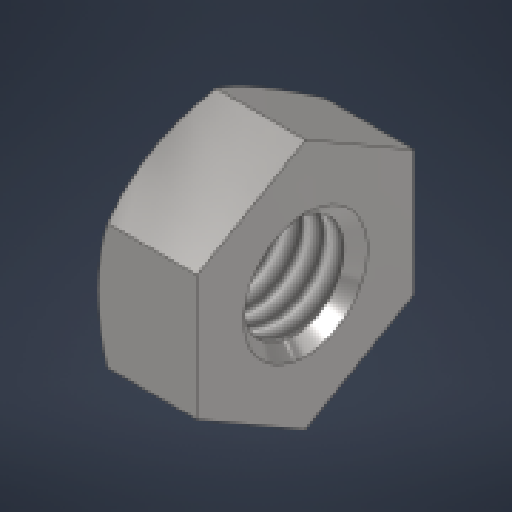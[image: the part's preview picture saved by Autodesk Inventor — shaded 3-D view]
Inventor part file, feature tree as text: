
AUTODESK INVENTOR PART (.ipt)
format: ipt  version: 2024 (Build 280153000, 153)  size: 225,792 bytes
history: native  units: mm
features: other x14, sketch x3, revolve x2, thread x1, extrude x1
ambient origin geometry x8: Origin, YZ Plane, XZ Plane, XY Plane, X Axis, Y Axis, Z Axis, Center Point
bodies: Solid1 (feature_tree)
feature tree (21):
  revolve  "Revolution1"  Angle=360.0deg
  revolve  "Revolution2"  [1 undecoded]
  thread  "Thread1"  [1 undecoded]
  extrude  "Extrusion1"  [1 undecoded]
  other  "cp_XY"
  other  "cp_YZ"
  other  "cp_ZX"
  other  "cp_X"
  other  "cp_Y"
  other  "cp_Z"
  other  "cp_Center"
  other  "nut_to_screw_XY"
  other  "nut_to_screw_YZ"
  other  "nut_to_screw_ZX"
  other  "nut_to_screw_X"
  other  "nut_to_screw_Y"
  other  "nut_to_screw_Z"
  other  "nut_to_screw_Center"
  sketch  "Sketch_1"  dims[d0=360.0deg d1=360.0deg]
  sketch  "Sketch_2"  dims[d2=2.442mm d3=0.0mm d4=3.2mm d5=0.0mm d6=0.0mm]
  sketch  "Sketch_3"
note: 3 required parameter values undecoded (feature->parameter linkage not recoverable at this tier; creation-order binding heuristic only, values carry confidence <= 0.55)